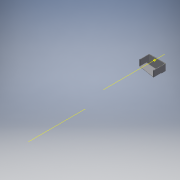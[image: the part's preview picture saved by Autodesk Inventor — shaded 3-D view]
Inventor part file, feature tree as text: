
AUTODESK INVENTOR PART (.ipt)
format: ipt  version: 2018 (Build 220112000, 112)  size: 520,192 bytes
history: native  units: mm
features: extrude x14, sketch x13, fillet x11, other x8, reference x5, plane x3, shell x1, projected_geometry x1
ambient origin geometry x8: Origin, YZ Plane, XZ Plane, XY Plane, X Axis, Y Axis, Z Axis, Center Point
bodies: Solid1 (feature_tree)
feature tree (56):
  extrude  "Extrusion1"  Depth=3.2mm
  extrude  "Extrusion2"  Depth=3.5mm
  extrude  "Extrusion3"  Depth=1.0mm
  sketch  "Sketch4"  dims[d7=3.5mm d8=2.0mm d9=0.0mm]
  other  "Work Axis2"
  other  "Work Axis1"
  plane  "Work Plane3"
  extrude  "Extrusion4"  Depth=2.0mm TaperAngle=0.0deg
  extrude  "Extrusion5"  Depth=7.0mm
  shell  "Shell1"  Thickness=15.2mm
  plane  "Work Plane4"
  sketch  "Sketch7"  dims[d18=1.0mm d19=45.0deg d20=1.5mm d21=30.0mm d22=0.0mm d23=0.0mm d24=0.0mm]
  extrude  "Extrusion6"  Depth=0.5mm
  extrude  "Extrusion7"  TaperAngle=45.0deg  [1 undecoded]
  fillet  "Fillet1"  Radius=1.5mm
  fillet  "Fillet2"  Radius=30.0mm
  fillet  "Fillet3"  [1 undecoded]
  extrude  "Extrusion8"  Depth=30.0mm TaperAngle=0.0deg
  fillet  "Fillet4"  Radius=1.0mm
  fillet  "Fillet5"  Radius=2.0mm
  fillet  "Fillet6"  Radius=2.0mm
  fillet  "Fillet7"  Radius=4.363323mm
  fillet  "Fillet8"  Radius=5.0mm
  fillet  "Fillet9"  Radius=3.0mm
  extrude  "Extrusion9"  Depth=3.0mm
  extrude  "Extrusion10"  Depth=3.0mm
  extrude  "Extrusion11"  Depth=1.0mm
  fillet  "Fillet10"  Radius=1.0mm
  fillet  "Fillet11"  Radius=2.0mm
  extrude  "Extrusion12"  Depth=1.0mm TaperAngle=0.0deg
  sketch  "Sketch1"  dims[d1=1.0mm d2=3.2mm]
  reference  "Reference1"
  sketch  "Sketch2"  dims[d3=3.5mm d4=3.5mm]
  reference  "Reference2"
  sketch  "Sketch3"  dims[d5=5.0mm d6=1.0mm]
  projected_geometry  "Projected Loop1"
  other  "Work Point1"
  plane  "Work Plane1"
  other  "Work Axis3"
  other  "Work Axis4"
  sketch  "Sketch5"  dims[d10=0.3mm d11=7.0mm d12=15.2mm d13=0.0mm]
  reference  "Reference3"
  reference  "Reference4"
  sketch  "Sketch6"  dims[d14=1.0mm d15=0.0mm d17=0.5mm]
  sketch  "Sketch9"  dims[d25=0.9mm d26=30.0mm d27=0.0mm d28=1.0mm d29=2.0mm d30=0.0mm d31=2.0mm d32=4.363323mm d33=5.0mm d34=3.0mm]
  sketch  "Sketch10"  dims[d35=2.0mm d36=0.0mm d37=3.0mm]
  sketch  "Sketch11"  dims[d38=3.0mm d39=3.0mm]
  sketch  "Sketch12"  dims[d40=3.0mm d41=1.0mm d42=1.0mm d43=2.0mm d44=0.0mm]
  sketch  "Sketch13"  dims[d45=1.0mm d46=0.0mm d47=1.0mm d48=0.0mm]
  sketch  "Sketch14"  dims[d49=1.0mm d50=1.0mm d51=0.0mm d52=0.0mm]
  reference  "Reference5"
  parser-record x1  (decoder bookkeeping rows leaked as tree rows — omitted from the tree; the rows remain in map.json)
  extrude  "Extruder Head.iam"  Depth=1.0mm
  other  "Radial-Cooling-Fan-5015-DC12V:1"
  other  "top:3"
  extrude  "Extruder:1"  TaperAngle=0.0deg  [1 undecoded]
note: 3 required parameter values undecoded (feature->parameter linkage not recoverable at this tier; creation-order binding heuristic only, values carry confidence <= 0.55)
note: 1 file-system path scrubbed to <path> (originals preserved in map.json)
